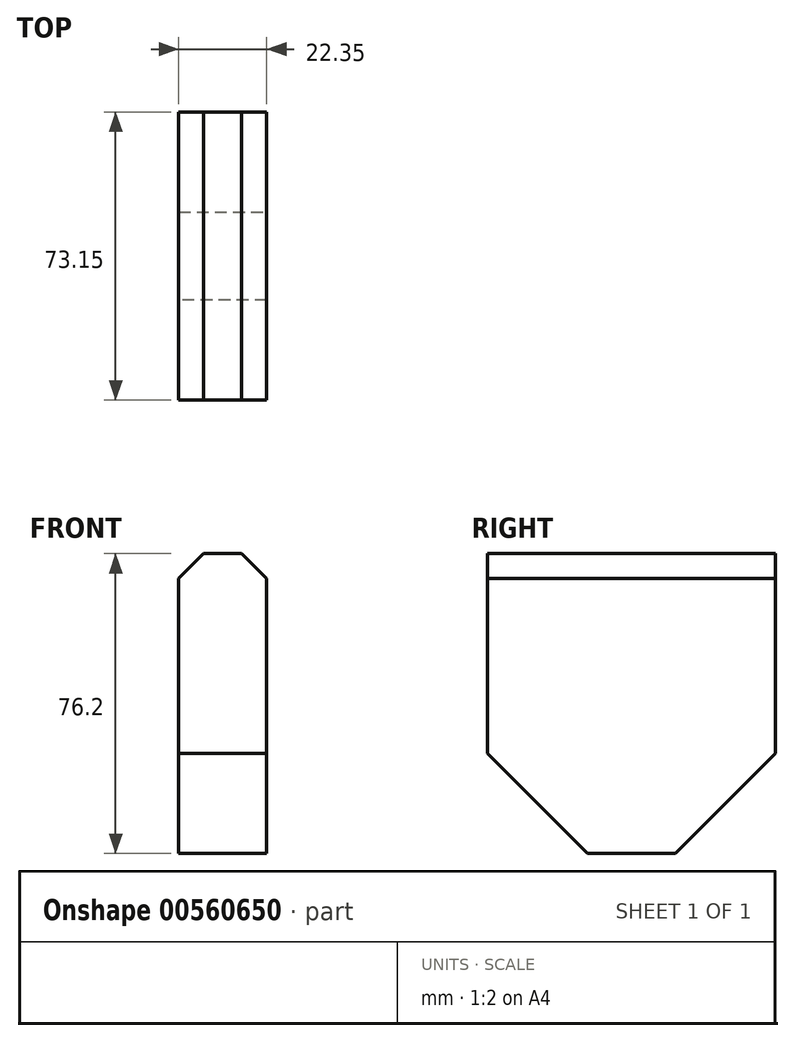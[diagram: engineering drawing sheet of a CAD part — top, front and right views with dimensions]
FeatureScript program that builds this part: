
annotation { "Feature Type Name" : "Feature", "Feature Type Description" : "" }
export const myFeature = defineFeature(function(context is Context, id is Id, definition is map)
    precondition{}
    {
        {
            var Q0;
            Q0=qCreatedBy(makeId("Right.planeOp"),FACE);
            var sketch = newSketch(context, id + "F0", { "sketchPlane" : qUnion([Q0])});
            skLineSegment(sketch, "E0", {"start": v(0, 0) * mm, "end": v(73.15, 0) * mm});
            skLineSegment(sketch, "E1", {"start": v(0, 0) * mm, "end": v(0, -76.2) * mm});
            skLineSegment(sketch, "E2", {"start": v(0, -76.2) * mm, "end": v(73.15, -76.2) * mm});
            skLineSegment(sketch, "E3", {"start": v(73.15, -76.2) * mm, "end": v(73.15, 0) * mm});
            skSolve(sketch);
        }
        {
            var Q0;
            Q0 = qSketchRegion(id + "F0", true);
            extrude(context, id + "F1", {"entities" : qUnion([Q0]), "depth" : 22.35 * mm, "offsetDistance" : 25.4 * mm});
        }
        {
            var Q0;
            Q0=makeQuery(id+"F1.opExtrude","SWEPT_EDGE",EDGE,{"disambiguationData":[OSD([sQuery(id+"F0.wireOp",EDGE,"E1"),sQuery(id+"F0.wireOp",EDGE,"E2")])]});
            var Q1;
            Q1=makeQuery(id+"F1.opExtrude","SWEPT_EDGE",EDGE,{"disambiguationData":[OSD([sQuery(id+"F0.wireOp",EDGE,"E2"),sQuery(id+"F0.wireOp",EDGE,"E3")])]});
            chamfer(context, id + "F2", {"entities" : qUnion([Q0, Q1]), "width" : 25.4 * mm, "tangentPropagation" : true});
        }
        {
            var Q0;
            Q0=makeQuery(id+"F1.opExtrude","CAP_EDGE",EDGE,{"disambiguationData":[OSD([sQuery(id+"F0.wireOp",EDGE,"E0")])],"isStart":true});
            var Q1;
            Q1=makeQuery(id+"F1.opExtrude","CAP_EDGE",EDGE,{"disambiguationData":[OSD([sQuery(id+"F0.wireOp",EDGE,"E0")])],"isStart":false});
            chamfer(context, id + "F3", {"entities" : qUnion([Q0, Q1]), "width" : 6.35 * mm, "tangentPropagation" : true});
        }
    });
